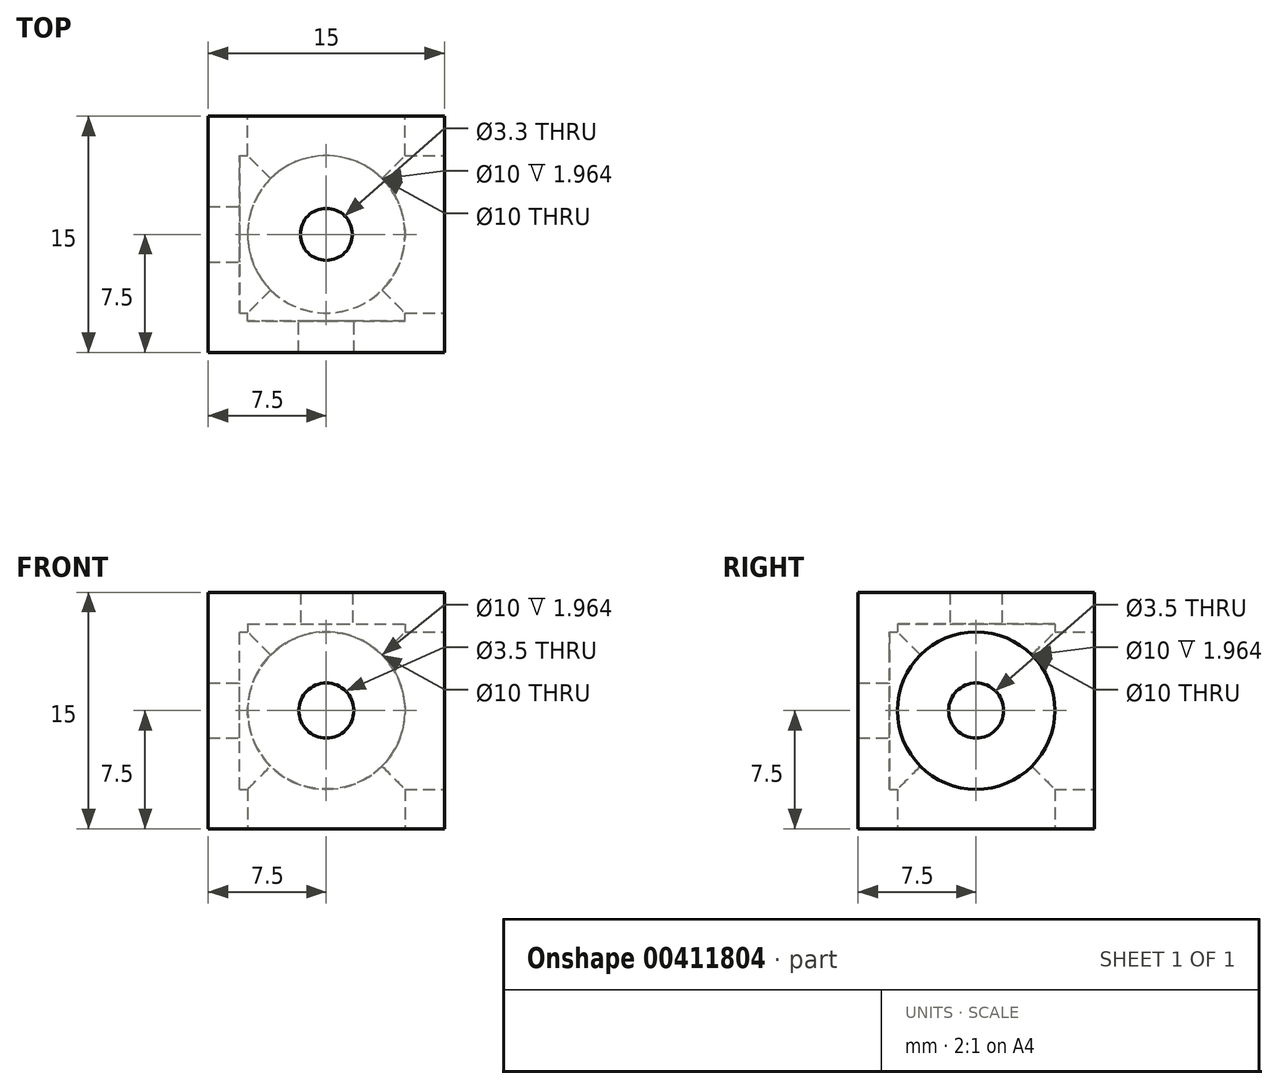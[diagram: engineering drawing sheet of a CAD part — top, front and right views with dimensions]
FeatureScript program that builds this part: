
annotation { "Feature Type Name" : "Feature", "Feature Type Description" : "" }
export const myFeature = defineFeature(function(context is Context, id is Id, definition is map)
    precondition{}
    {
        {
            var Q0;
            Q0=qCreatedBy(makeId("Front.planeOp"),FACE);
            var sketch = newSketch(context, id + "F0", { "sketchPlane" : qUnion([Q0])});
            skLineSegment(sketch, "E0.bottom", {"start": v(-7.5, 7.5) * mm, "end": v(7.5, 7.5) * mm});
            skLineSegment(sketch, "E0.top", {"start": v(-7.5, -7.5) * mm, "end": v(7.5, -7.5) * mm});
            skLineSegment(sketch, "E0.left", {"start": v(-7.5, 7.5) * mm, "end": v(-7.5, -7.5) * mm});
            skLineSegment(sketch, "E0.right", {"start": v(7.5, 7.5) * mm, "end": v(7.5, -7.5) * mm});
            skCircle(sketch, "E1", {"center": v(0, 0) * mm, "radius": 1.75 * mm});
            skSolve(sketch);
        }
        {
            var Q0;
            Q0 = qSketchRegion(id + "F0", true);
            extrude(context, id + "F1", {"entities" : qUnion([Q0]), "depth" : 15 * mm});
        }
        {
            var Q0;
            Q0=makeQuery(id+"F0.imprint","IMPRINT",FACE,{"disambiguationData":[TD([[makeQuery(id+"F0.imprint","IMPRINT",EDGE,{"derivedFrom":sQuery(id+"F0.wireOp",EDGE,"E0.bottom")}),-1.0]])]});
            var sketch = newSketch(context, id + "F2", { "sketchPlane" : qUnion([Q0])});
            skCircle(sketch, "E2", {"center": v(0, 0) * mm, "radius": 5 * mm});
            skSolve(sketch);
        }
        {
            var Q0;
            Q0 = qSketchRegion(id + "F2", true);
            var Q1;
            Q1=sQuery(id+"F2.wireOp",EDGE,"E2");
            extrude(context, id + "F3", {"entities" : qUnion([Q0]), "operationType" : NewBodyOperationType.REMOVE, "surfaceEntities" : qUnion([Q1]), "depth" : 13 * mm});
        }
        {
            var Q0;
            Q0=makeQuery(id+"F1.opExtrude","SWEPT_FACE",FACE,{"disambiguationData":[OSD([sQuery(id+"F0.wireOp",EDGE,"E0.right")])]});
            var sketch = newSketch(context, id + "F4", { "sketchPlane" : qUnion([Q0])});
            skCircle(sketch, "E3", {"center": v(-7.5, 0) * mm, "radius": 1.75 * mm});
            skCircle(sketch, "E4", {"center": v(-7.5, 0) * mm, "radius": 5 * mm});
            skSolve(sketch);
        }
        {
            var Q0;
            Q0=makeQuery(id+"F4.imprint","IMPRINT",FACE,{"disambiguationData":[TD([[makeQuery(id+"F4.imprint","IMPRINT",EDGE,{"derivedFrom":sQuery(id+"F4.wireOp",EDGE,"E3")}),1.0]])]});
            extrude(context, id + "F5", {"entities" : qUnion([Q0]), "operationType" : NewBodyOperationType.REMOVE, "oppositeDirection" : true, "depth" : 15 * mm});
        }
        {
            var Q0;
            Q0 = qSketchRegion(id + "F4", true);
            extrude(context, id + "F6", {"entities" : qUnion([Q0]), "operationType" : NewBodyOperationType.REMOVE, "oppositeDirection" : true, "depth" : 13 * mm});
        }
        {
            var Q0;
            Q0=makeQuery(id+"F1.opExtrude","SWEPT_FACE",FACE,{"disambiguationData":[OSD([sQuery(id+"F0.wireOp",EDGE,"E0.top")])]});
            var sketch = newSketch(context, id + "F7", { "sketchPlane" : qUnion([Q0])});
            skCircle(sketch, "E5", {"center": v(0, 7.5) * mm, "radius": 1.65 * mm});
            skCircle(sketch, "E6", {"center": v(0, 7.5) * mm, "radius": 5 * mm});
            skSolve(sketch);
        }
        {
            var Q0;
            Q0=makeQuery(id+"F7.imprint","IMPRINT",FACE,{"disambiguationData":[TD([[makeQuery(id+"F7.imprint","IMPRINT",EDGE,{"derivedFrom":sQuery(id+"F7.wireOp",EDGE,"E5")}),1.0]])]});
            extrude(context, id + "F8", {"entities" : qUnion([Q0]), "operationType" : NewBodyOperationType.REMOVE, "oppositeDirection" : true, "depth" : 15 * mm});
        }
        {
            var Q0;
            Q0=makeQuery(id+"F7.imprint","IMPRINT",FACE,{"disambiguationData":[TD([[makeQuery(id+"F7.imprint","IMPRINT",EDGE,{"derivedFrom":sQuery(id+"F7.wireOp",EDGE,"E5")}),-1.0]])]});
            var Q1;
            Q1=sQuery(id+"F7.wireOp",EDGE,"E6");
            extrude(context, id + "F9", {"entities" : qUnion([Q0]), "operationType" : NewBodyOperationType.REMOVE, "surfaceEntities" : qUnion([Q1]), "oppositeDirection" : true, "depth" : 13 * mm});
        }
    });
